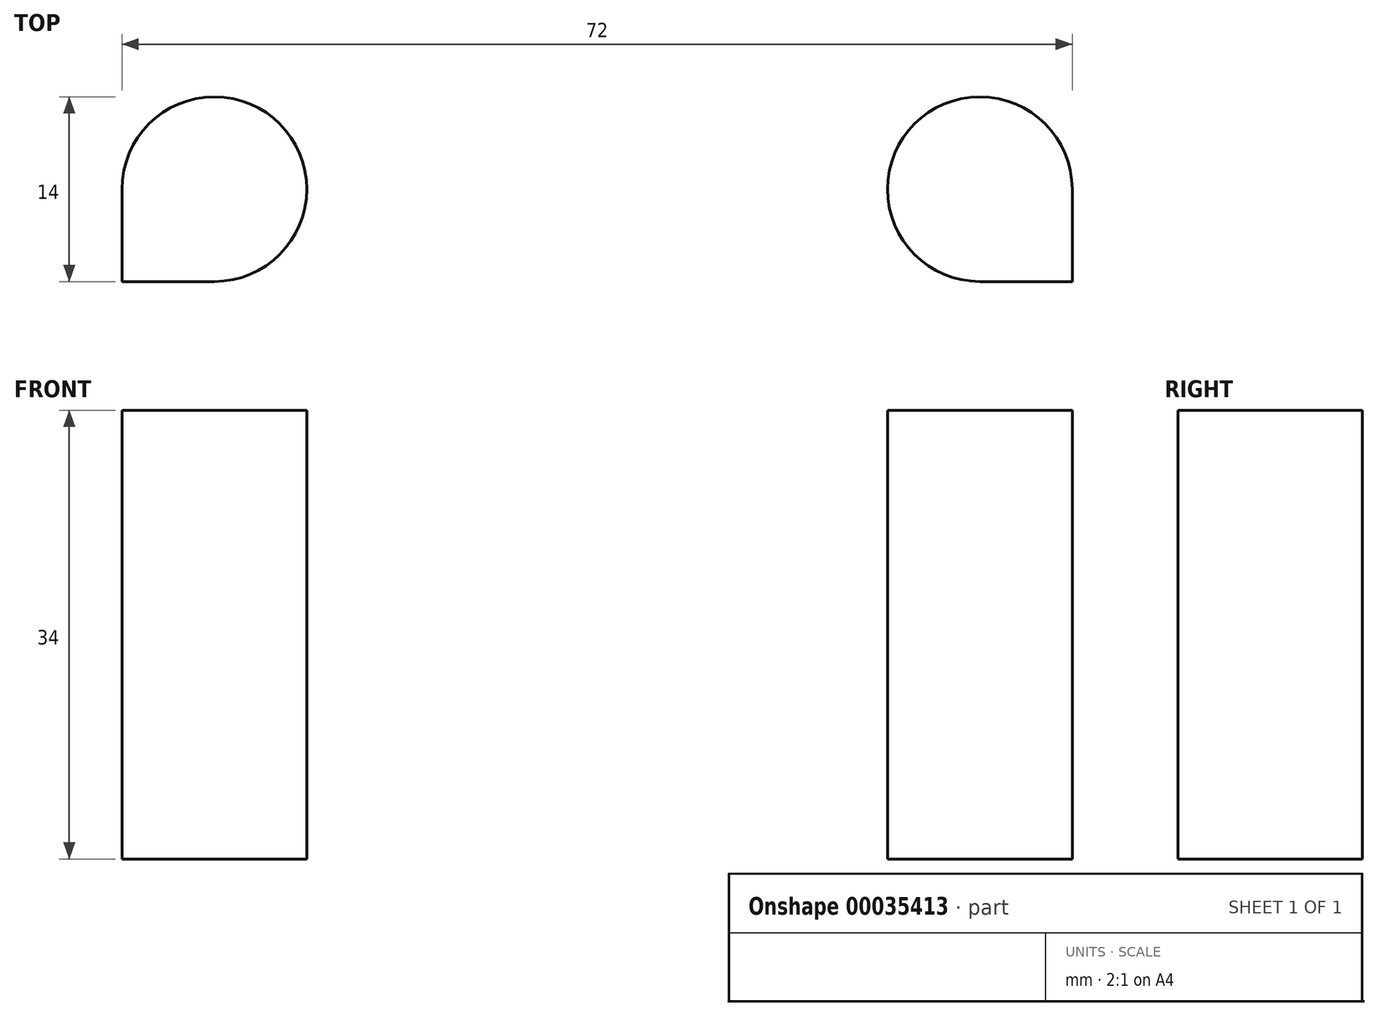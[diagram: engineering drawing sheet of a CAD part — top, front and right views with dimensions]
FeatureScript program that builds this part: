
annotation { "Feature Type Name" : "Feature", "Feature Type Description" : "" }
export const myFeature = defineFeature(function(context is Context, id is Id, definition is map)
    precondition{}
    {
        {
            var Q0;
            Q0=qCreatedBy(makeId("Top.planeOp"),FACE);
            var sketch = newSketch(context, id + "F0", { "sketchPlane" : qUnion([Q0])});
            skLineSegment(sketch, "E0", {"start": v(0, 0) * mm, "end": v(-72, 0) * mm});
            skLineSegment(sketch, "E1", {"start": v(-72, 0) * mm, "end": v(-72, 14) * mm});
            skLineSegment(sketch, "E2", {"start": v(-72, 14) * mm, "end": v(0, 14) * mm});
            skLineSegment(sketch, "E3", {"start": v(0, 14) * mm, "end": v(0, 0) * mm});
            skLineSegment(sketch, "E4", {"start": v(-72, 0) * mm, "end": v(-65, 0) * mm});
            skLineSegment(sketch, "E5", {"start": v(-65, 0) * mm, "end": v(-65, 7) * mm});
            skLineSegment(sketch, "E6", {"start": v(0, 0) * mm, "end": v(-7, 0) * mm});
            skLineSegment(sketch, "E7", {"start": v(-7, 0) * mm, "end": v(-7, 7) * mm});
            skCircle(sketch, "E8", {"center": v(-7, 7) * mm, "radius": 7 * mm});
            skCircle(sketch, "E9", {"center": v(-65, 7) * mm, "radius": 7 * mm});
            skSolve(sketch);
        }
        {
            var Q0;
            {var subQ0=sQuery(id+"F0.wireOp",EDGE,"E9");var subQ3=makeQuery(id+"F0.imprint","INTERSECT",VERTEX,{"derivedFrom":[sQuery(id+"F0.wireOp",EDGE,"E1"),subQ0]});Q0=makeQuery(id+"F0.imprint","IMPRINT",FACE,{"disambiguationData":[TD([[makeQuery(id+"F0.imprint","IMPRINT",EDGE,{"disambiguationData":[TD([[subQ3,1.0]])],"derivedFrom":subQ0}),1.0]])]});}
            var Q1;
            {var subQ3=sQuery(id+"F0.wireOp",EDGE,"E0");Q1=makeQuery(id+"F0.imprint","IMPRINT",FACE,{"disambiguationData":[TD([[makeQuery(id+"F0.imprint","IMPRINT",EDGE,{"derivedFrom":subQ3}),-1.0]])]});}
            var Q2;
            {var subQ0=sQuery(id+"F0.wireOp",EDGE,"E8");var subQ3=makeQuery(id+"F0.imprint","INTERSECT",VERTEX,{"derivedFrom":[sQuery(id+"F0.wireOp",EDGE,"E2"),subQ0]});Q2=makeQuery(id+"F0.imprint","IMPRINT",FACE,{"disambiguationData":[TD([[makeQuery(id+"F0.imprint","IMPRINT",EDGE,{"disambiguationData":[TD([[subQ3,1.0]])],"derivedFrom":subQ0}),1.0]])]});}
            extrude(context, id + "F1", {"entities" : qUnion([Q0, Q1, Q2]), "depth" : 34 * mm});
        }
    });
